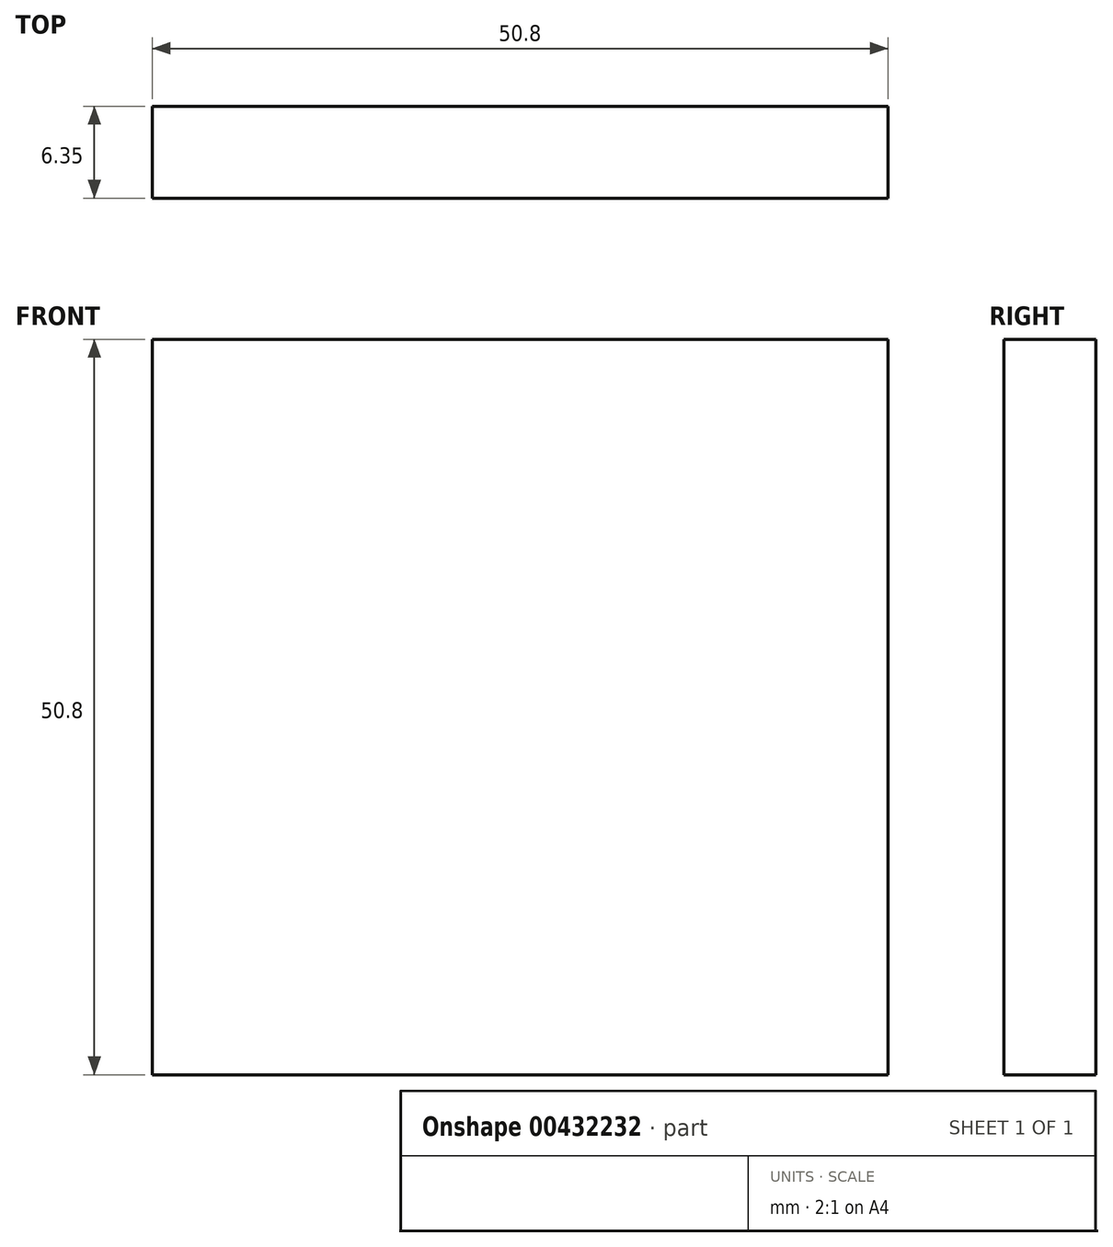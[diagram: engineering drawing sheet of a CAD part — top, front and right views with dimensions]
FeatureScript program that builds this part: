
annotation { "Feature Type Name" : "Feature", "Feature Type Description" : "" }
export const myFeature = defineFeature(function(context is Context, id is Id, definition is map)
    precondition{}
    {
        {
            var Q0;
            Q0=qCreatedBy(makeId("Front.planeOp"),FACE);
            var sketch = newSketch(context, id + "F0", { "sketchPlane" : qUnion([Q0])});
            skLineSegment(sketch, "E0", {"start": v(0, 0) * mm, "end": v(50.8, 0) * mm});
            skLineSegment(sketch, "E1", {"start": v(50.8, 0) * mm, "end": v(50.8, 50.8) * mm});
            skLineSegment(sketch, "E2", {"start": v(50.8, 50.8) * mm, "end": v(0, 50.8) * mm});
            skLineSegment(sketch, "E3", {"start": v(0, 50.8) * mm, "end": v(0, 0) * mm});
            skSolve(sketch);
        }
        {
            var Q0;
            Q0 = qSketchRegion(id + "F0", true);
            extrude(context, id + "F1", {"entities" : qUnion([Q0]), "depth" : 6.35 * mm});
        }
    });
